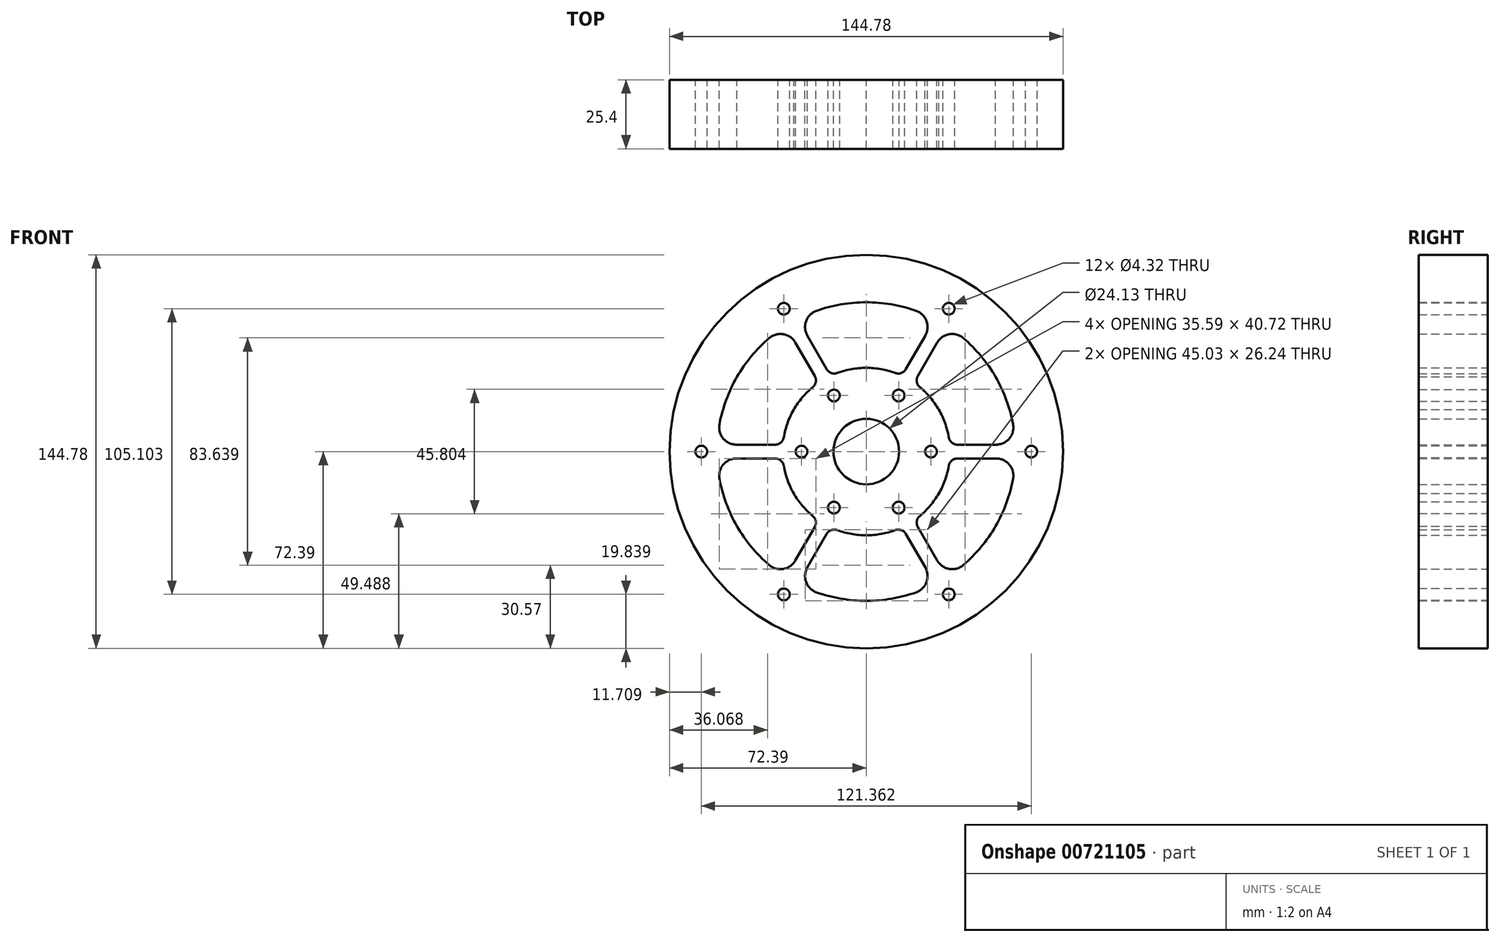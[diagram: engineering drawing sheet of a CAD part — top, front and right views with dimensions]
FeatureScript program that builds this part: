
annotation { "Feature Type Name" : "Feature", "Feature Type Description" : "" }
export const myFeature = defineFeature(function(context is Context, id is Id, definition is map)
    precondition{}
    {
        {
            var Q0;
            Q0=qCreatedBy(makeId("Front.planeOp"),FACE);
            var sketch = newSketch(context, id + "F0", { "sketchPlane" : qUnion([Q0])});
            skCircle(sketch, "E0", {"center": v(0, 0) * mm, "radius": 12.07 * mm});
            skCircle(sketch, "E1", {"center": v(0, 0) * mm, "radius": 72.4 * mm});
            skArc(sketch, "E2", {"start": v(10.72, 28.9) * mm, "mid": v(5.44, 30.32) * mm, "end": v(0, 30.84) * mm});
            skArc(sketch, "E3", {"start": v(18.26, 51.81) * mm, "mid": v(9.26, 54.13) * mm, "end": v(0, 54.94) * mm});
            skPoint(sketch, "E4.visualSharp", {"position": v(25.27, 48.85) * mm});
            skArc(sketch, "E4.filletArc", {"start": v(21.68, 42.64) * mm, "mid": v(22.13, 48.03) * mm, "end": v(18.26, 51.81) * mm});
            skArc(sketch, "E5.MirrorCS", {"start": v(-18.26, 51.81) * mm, "mid": v(-9.26, 54.13) * mm, "end": v(0, 54.94) * mm});
            skArc(sketch, "E6.MirrorCS", {"start": v(-21.68, 42.64) * mm, "mid": v(-22.13, 48.03) * mm, "end": v(-18.26, 51.81) * mm});
            skArc(sketch, "E7.MirrorCS", {"start": v(-10.72, 28.9) * mm, "mid": v(-5.44, 30.32) * mm, "end": v(0, 30.84) * mm});
            skLineSegment(sketch, "E8", {"start": v(-21.68, 42.64) * mm, "end": v(-14.55, 30.29) * mm});
            skLineSegment(sketch, "E9", {"start": v(21.68, 42.64) * mm, "end": v(14.55, 30.29) * mm});
            skPoint(sketch, "E10.visualSharp", {"position": v(-13.17, 27.88) * mm});
            skArc(sketch, "E10.filletArc", {"start": v(-14.55, 30.29) * mm, "mid": v(-12.89, 28.9) * mm, "end": v(-10.72, 28.9) * mm});
            skPoint(sketch, "E11.visualSharp", {"position": v(13.17, 27.88) * mm});
            skArc(sketch, "E11.filletArc", {"start": v(10.72, 28.9) * mm, "mid": v(12.89, 28.9) * mm, "end": v(14.55, 30.29) * mm});
            skPoint(sketch, "E12.1.0", {"position": v(-30.73, 2.54) * mm});
            skArc(sketch, "E12.1.1", {"start": v(-35.74, 41.72) * mm, "mid": v(-42.24, 35.08) * mm, "end": v(-47.58, 27.47) * mm});
            skArc(sketch, "E12.1.2", {"start": v(-54, 10.1) * mm, "mid": v(-51.5, 19.04) * mm, "end": v(-47.58, 27.47) * mm});
            skPoint(sketch, "E12.1.3", {"position": v(-29.67, 46.3) * mm});
            skLineSegment(sketch, "E12.1.4", {"start": v(-26.08, 40.1) * mm, "end": v(-18.95, 27.75) * mm});
            skArc(sketch, "E12.1.5", {"start": v(-26.08, 40.1) * mm, "mid": v(-30.53, 43.19) * mm, "end": v(-35.74, 41.72) * mm});
            skArc(sketch, "E12.1.6", {"start": v(-19.66, 23.73) * mm, "mid": v(-23.54, 19.87) * mm, "end": v(-26.7, 15.42) * mm});
            skArc(sketch, "E12.1.7", {"start": v(-19.66, 23.73) * mm, "mid": v(-18.58, 25.6) * mm, "end": v(-18.95, 27.75) * mm});
            skLineSegment(sketch, "E12.1.8", {"start": v(-47.77, 2.54) * mm, "end": v(-33.5, 2.54) * mm});
            skArc(sketch, "E12.1.9", {"start": v(-30.38, 5.17) * mm, "mid": v(-28.98, 10.45) * mm, "end": v(-26.7, 15.42) * mm});
            skArc(sketch, "E12.1.10", {"start": v(-33.5, 2.54) * mm, "mid": v(-31.47, 3.28) * mm, "end": v(-30.38, 5.17) * mm});
            skPoint(sketch, "E12.1.11", {"position": v(-17.57, 25.34) * mm});
            skArc(sketch, "E12.1.12", {"start": v(-47.77, 2.54) * mm, "mid": v(-52.66, 4.85) * mm, "end": v(-54, 10.1) * mm});
            skPoint(sketch, "E12.2.0", {"position": v(-17.57, -25.34) * mm});
            skArc(sketch, "E12.2.1", {"start": v(-54, -10.1) * mm, "mid": v(-51.5, -19.04) * mm, "end": v(-47.58, -27.47) * mm});
            skArc(sketch, "E12.2.2", {"start": v(-35.74, -41.72) * mm, "mid": v(-42.24, -35.08) * mm, "end": v(-47.58, -27.47) * mm});
            skPoint(sketch, "E12.2.3", {"position": v(-54.94, -2.54) * mm});
            skLineSegment(sketch, "E12.2.4", {"start": v(-47.77, -2.54) * mm, "end": v(-33.5, -2.54) * mm});
            skArc(sketch, "E12.2.5", {"start": v(-47.77, -2.54) * mm, "mid": v(-52.66, -4.85) * mm, "end": v(-54, -10.1) * mm});
            skArc(sketch, "E12.2.6", {"start": v(-30.38, -5.17) * mm, "mid": v(-28.98, -10.45) * mm, "end": v(-26.7, -15.42) * mm});
            skArc(sketch, "E12.2.7", {"start": v(-30.38, -5.17) * mm, "mid": v(-31.47, -3.28) * mm, "end": v(-33.5, -2.54) * mm});
            skLineSegment(sketch, "E12.2.8", {"start": v(-26.08, -40.1) * mm, "end": v(-18.95, -27.75) * mm});
            skArc(sketch, "E12.2.9", {"start": v(-19.66, -23.73) * mm, "mid": v(-23.54, -19.87) * mm, "end": v(-26.7, -15.42) * mm});
            skArc(sketch, "E12.2.10", {"start": v(-18.95, -27.75) * mm, "mid": v(-18.58, -25.6) * mm, "end": v(-19.66, -23.73) * mm});
            skPoint(sketch, "E12.2.11", {"position": v(-30.73, -2.54) * mm});
            skArc(sketch, "E12.2.12", {"start": v(-26.08, -40.1) * mm, "mid": v(-30.53, -43.19) * mm, "end": v(-35.74, -41.72) * mm});
            skPoint(sketch, "E12.3.0", {"position": v(13.17, -27.88) * mm});
            skArc(sketch, "E12.3.1", {"start": v(-18.26, -51.81) * mm, "mid": v(-9.26, -54.13) * mm, "end": v(0, -54.94) * mm});
            skArc(sketch, "E12.3.2", {"start": v(18.26, -51.81) * mm, "mid": v(9.26, -54.13) * mm, "end": v(0, -54.94) * mm});
            skPoint(sketch, "E12.3.3", {"position": v(-25.27, -48.85) * mm});
            skLineSegment(sketch, "E12.3.4", {"start": v(-21.68, -42.64) * mm, "end": v(-14.55, -30.29) * mm});
            skArc(sketch, "E12.3.5", {"start": v(-21.68, -42.64) * mm, "mid": v(-22.13, -48.03) * mm, "end": v(-18.26, -51.81) * mm});
            skArc(sketch, "E12.3.6", {"start": v(-10.72, -28.9) * mm, "mid": v(-5.44, -30.32) * mm, "end": v(0, -30.84) * mm});
            skArc(sketch, "E12.3.7", {"start": v(-10.72, -28.9) * mm, "mid": v(-12.89, -28.9) * mm, "end": v(-14.55, -30.29) * mm});
            skLineSegment(sketch, "E12.3.8", {"start": v(21.68, -42.64) * mm, "end": v(14.55, -30.29) * mm});
            skArc(sketch, "E12.3.9", {"start": v(10.72, -28.9) * mm, "mid": v(5.44, -30.32) * mm, "end": v(0, -30.84) * mm});
            skArc(sketch, "E12.3.10", {"start": v(14.55, -30.29) * mm, "mid": v(12.89, -28.9) * mm, "end": v(10.72, -28.9) * mm});
            skPoint(sketch, "E12.3.11", {"position": v(-13.17, -27.88) * mm});
            skArc(sketch, "E12.3.12", {"start": v(21.68, -42.64) * mm, "mid": v(22.13, -48.03) * mm, "end": v(18.26, -51.81) * mm});
            skPoint(sketch, "E12.4.0", {"position": v(30.73, -2.54) * mm});
            skArc(sketch, "E12.4.1", {"start": v(35.74, -41.72) * mm, "mid": v(42.24, -35.08) * mm, "end": v(47.58, -27.47) * mm});
            skArc(sketch, "E12.4.2", {"start": v(54, -10.1) * mm, "mid": v(51.5, -19.04) * mm, "end": v(47.58, -27.47) * mm});
            skPoint(sketch, "E12.4.3", {"position": v(29.67, -46.3) * mm});
            skLineSegment(sketch, "E12.4.4", {"start": v(26.08, -40.1) * mm, "end": v(18.95, -27.75) * mm});
            skArc(sketch, "E12.4.5", {"start": v(26.08, -40.1) * mm, "mid": v(30.53, -43.19) * mm, "end": v(35.74, -41.72) * mm});
            skArc(sketch, "E12.4.6", {"start": v(19.66, -23.73) * mm, "mid": v(23.54, -19.87) * mm, "end": v(26.7, -15.42) * mm});
            skArc(sketch, "E12.4.7", {"start": v(19.66, -23.73) * mm, "mid": v(18.58, -25.6) * mm, "end": v(18.95, -27.75) * mm});
            skLineSegment(sketch, "E12.4.8", {"start": v(47.77, -2.54) * mm, "end": v(33.5, -2.54) * mm});
            skArc(sketch, "E12.4.9", {"start": v(30.38, -5.17) * mm, "mid": v(28.98, -10.45) * mm, "end": v(26.7, -15.42) * mm});
            skArc(sketch, "E12.4.10", {"start": v(33.5, -2.54) * mm, "mid": v(31.47, -3.28) * mm, "end": v(30.38, -5.17) * mm});
            skPoint(sketch, "E12.4.11", {"position": v(17.57, -25.34) * mm});
            skArc(sketch, "E12.4.12", {"start": v(47.77, -2.54) * mm, "mid": v(52.66, -4.85) * mm, "end": v(54, -10.1) * mm});
            skPoint(sketch, "E12.5.0", {"position": v(17.57, 25.34) * mm});
            skArc(sketch, "E12.5.1", {"start": v(54, 10.1) * mm, "mid": v(51.5, 19.04) * mm, "end": v(47.58, 27.47) * mm});
            skArc(sketch, "E12.5.2", {"start": v(35.74, 41.72) * mm, "mid": v(42.24, 35.08) * mm, "end": v(47.58, 27.47) * mm});
            skPoint(sketch, "E12.5.3", {"position": v(54.94, 2.54) * mm});
            skLineSegment(sketch, "E12.5.4", {"start": v(47.77, 2.54) * mm, "end": v(33.5, 2.54) * mm});
            skArc(sketch, "E12.5.5", {"start": v(47.77, 2.54) * mm, "mid": v(52.66, 4.85) * mm, "end": v(54, 10.1) * mm});
            skArc(sketch, "E12.5.6", {"start": v(30.38, 5.17) * mm, "mid": v(28.98, 10.45) * mm, "end": v(26.7, 15.42) * mm});
            skArc(sketch, "E12.5.7", {"start": v(30.38, 5.17) * mm, "mid": v(31.47, 3.28) * mm, "end": v(33.5, 2.54) * mm});
            skLineSegment(sketch, "E12.5.8", {"start": v(26.08, 40.1) * mm, "end": v(18.95, 27.75) * mm});
            skArc(sketch, "E12.5.9", {"start": v(19.66, 23.73) * mm, "mid": v(23.54, 19.87) * mm, "end": v(26.7, 15.42) * mm});
            skArc(sketch, "E12.5.10", {"start": v(18.95, 27.75) * mm, "mid": v(18.58, 25.6) * mm, "end": v(19.66, 23.73) * mm});
            skPoint(sketch, "E12.5.11", {"position": v(30.73, 2.54) * mm});
            skArc(sketch, "E12.5.12", {"start": v(26.08, 40.1) * mm, "mid": v(30.53, 43.19) * mm, "end": v(35.74, 41.72) * mm});
            skCircle(sketch, "E13", {"center": v(-23.81, 0) * mm, "radius": 2.16 * mm});
            skCircle(sketch, "E14.1.0", {"center": v(-11.9, -20.62) * mm, "radius": 2.16 * mm});
            skCircle(sketch, "E14.2.0", {"center": v(11.9, -20.62) * mm, "radius": 2.16 * mm});
            skCircle(sketch, "E14.3.0", {"center": v(23.81, 0) * mm, "radius": 2.16 * mm});
            skCircle(sketch, "E14.4.0", {"center": v(11.9, 20.62) * mm, "radius": 2.16 * mm});
            skCircle(sketch, "E14.5.0", {"center": v(-11.9, 20.62) * mm, "radius": 2.16 * mm});
            skCircle(sketch, "E15", {"center": v(30.34, -52.55) * mm, "radius": 2.16 * mm});
            skCircle(sketch, "E16.1.0", {"center": v(60.68, 0) * mm, "radius": 2.16 * mm});
            skCircle(sketch, "E16.2.0", {"center": v(30.34, 52.55) * mm, "radius": 2.16 * mm});
            skCircle(sketch, "E16.3.0", {"center": v(-30.34, 52.55) * mm, "radius": 2.16 * mm});
            skCircle(sketch, "E16.4.0", {"center": v(-60.68, 0) * mm, "radius": 2.16 * mm});
            skCircle(sketch, "E16.5.0", {"center": v(-30.34, -52.55) * mm, "radius": 2.16 * mm});
            skSolve(sketch);
        }
        {
            var Q0;
            Q0=makeQuery(id+"F0.imprint","IMPRINT",FACE,{"disambiguationData":[TD([[makeQuery(id+"F0.imprint","IMPRINT",EDGE,{"derivedFrom":sQuery(id+"F0.wireOp",EDGE,"E0")}),-1.0]])]});
            extrude(context, id + "F1", {"entities" : qUnion([Q0]), "depth" : 25.4 * mm, "offsetDistance" : 25.4 * mm});
        }
    });
